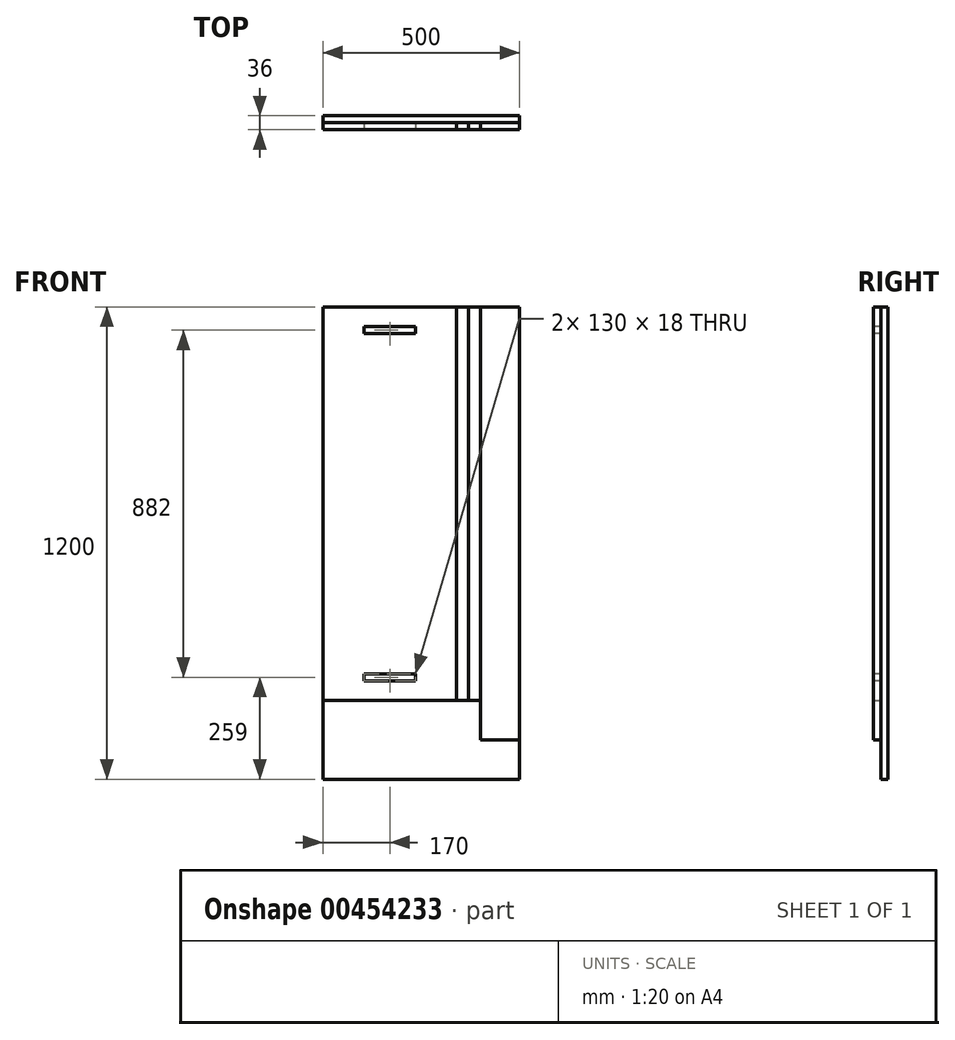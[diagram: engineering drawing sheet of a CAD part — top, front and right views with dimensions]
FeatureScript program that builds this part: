
annotation { "Feature Type Name" : "Feature", "Feature Type Description" : "" }
export const myFeature = defineFeature(function(context is Context, id is Id, definition is map)
    precondition{}
    {
        {
            var Q0;
            Q0=qCreatedBy(makeId("Front.planeOp"),FACE);
            var sketch = newSketch(context, id + "F0", { "sketchPlane" : qUnion([Q0])});
            skLineSegment(sketch, "E0.bottom", {"start": v(-250, -600) * mm, "end": v(250, -600) * mm});
            skLineSegment(sketch, "E0.top", {"start": v(-250, 600) * mm, "end": v(250, 600) * mm});
            skLineSegment(sketch, "E0.left", {"start": v(-250, -600) * mm, "end": v(-250, 600) * mm});
            skLineSegment(sketch, "E0.right", {"start": v(250, -600) * mm, "end": v(250, 600) * mm});
            skPoint(sketch, "E0.middle", {"position": v(0, 0) * mm});
            skSolve(sketch);
        }
        {
            var Q0;
            Q0=qSketchRegion(id+"F0",true);
            extrude(context, id + "F1", {"entities" : qUnion([Q0]), "depth" : 18 * mm});
        }
        {
            var Q0;
            Q0=makeQuery(id+"F1.opExtrude","CAP_FACE",FACE,{"disambiguationData":[OSD([sQuery(id+"F0.wireOp",EDGE,"E0.bottom"),sQuery(id+"F0.wireOp",EDGE,"E0.top"),sQuery(id+"F0.wireOp",EDGE,"E0.left"),sQuery(id+"F0.wireOp",EDGE,"E0.right")])],"isStart":false});
            var sketch = newSketch(context, id + "F2", { "sketchPlane" : qUnion([Q0])});
            skLineSegment(sketch, "E1.bottom", {"start": v(-250, 600) * mm, "end": v(90, 600) * mm});
            skLineSegment(sketch, "E1.top", {"start": v(-250, -400) * mm, "end": v(90, -400) * mm});
            skLineSegment(sketch, "E1.left", {"start": v(-250, 600) * mm, "end": v(-250, -400) * mm});
            skLineSegment(sketch, "E1.right", {"start": v(90, 600) * mm, "end": v(90, -400) * mm});
            skLineSegment(sketch, "E2.bottom", {"start": v(90, -400) * mm, "end": v(120, -400) * mm});
            skLineSegment(sketch, "E2.top", {"start": v(90, 600) * mm, "end": v(120, 600) * mm});
            skLineSegment(sketch, "E2.left", {"start": v(90, -400) * mm, "end": v(90, 600) * mm});
            skLineSegment(sketch, "E2.right", {"start": v(120, -400) * mm, "end": v(120, 600) * mm});
            skLineSegment(sketch, "E3.bottom", {"start": v(120, -400) * mm, "end": v(150, -400) * mm});
            skLineSegment(sketch, "E3.top", {"start": v(120, 600) * mm, "end": v(150, 600) * mm});
            skLineSegment(sketch, "E3.right", {"start": v(150, -400) * mm, "end": v(150, 600) * mm});
            skLineSegment(sketch, "E4.bottom", {"start": v(250, 600) * mm, "end": v(150, 600) * mm});
            skLineSegment(sketch, "E4.top", {"start": v(250, -500) * mm, "end": v(150, -500) * mm});
            skLineSegment(sketch, "E4.left", {"start": v(250, 600) * mm, "end": v(250, -500) * mm});
            skLineSegment(sketch, "E4.right", {"start": v(150, 600) * mm, "end": v(150, -500) * mm});
            skSolve(sketch);
        }
        {
            var Q0;
            Q0=makeQuery(id+"F2.imprint","IMPRINT",FACE,{"disambiguationData":[TD([[makeQuery(id+"F2.imprint","IMPRINT",EDGE,{"derivedFrom":sQuery(id+"F2.wireOp",EDGE,"E1.bottom")}),-1.0]])]});
            extrude(context, id + "F3", {"entities" : qUnion([Q0]), "depth" : 18 * mm});
        }
        {
            var Q0;
            Q0=makeQuery(id+"F2.imprint","IMPRINT",FACE,{"disambiguationData":[TD([[makeQuery(id+"F2.imprint","IMPRINT",EDGE,{"derivedFrom":sQuery(id+"F2.wireOp",EDGE,"E2.bottom")}),1.0]])]});
            extrude(context, id + "F4", {"entities" : qUnion([Q0]), "depth" : 18 * mm});
        }
        {
            var Q0;
            {var subQ0=sQuery(id+"F2.wireOp",EDGE,"E3.bottom");Q0=makeQuery(id+"F2.imprint","IMPRINT",FACE,{"disambiguationData":[TD([[makeQuery(id+"F2.imprint","IMPRINT",EDGE,{"derivedFrom":subQ0}),1.0]])]});}
            extrude(context, id + "F5", {"entities" : qUnion([Q0]), "depth" : 18 * mm});
        }
        {
            var Q0;
            {var subQ2=sQuery(id+"F2.wireOp",EDGE,"E4.bottom");Q0=makeQuery(id+"F2.imprint","IMPRINT",FACE,{"disambiguationData":[TD([[makeQuery(id+"F2.imprint","IMPRINT",EDGE,{"derivedFrom":subQ2}),-1.0]])]});}
            extrude(context, id + "F6", {"entities" : qUnion([Q0]), "depth" : 18 * mm});
        }
        {
            var Q0;
            Q0=makeQuery(id+"F3.opExtrude","CAP_FACE",FACE,{"disambiguationData":[OSD([sQuery(id+"F2.wireOp",EDGE,"E1.bottom"),sQuery(id+"F2.wireOp",EDGE,"E1.top"),sQuery(id+"F2.wireOp",EDGE,"E1.left"),sQuery(id+"F2.wireOp",EDGE,"E2.left")])],"isStart":false});
            var sketch = newSketch(context, id + "F7", { "sketchPlane" : qUnion([Q0])});
            skLineSegment(sketch, "E5.bottom", {"start": v(-145, 550) * mm, "end": v(-15, 550) * mm});
            skLineSegment(sketch, "E5.top", {"start": v(-145, 532) * mm, "end": v(-15, 532) * mm});
            skLineSegment(sketch, "E5.left", {"start": v(-145, 550) * mm, "end": v(-145, 532) * mm});
            skLineSegment(sketch, "E5.right", {"start": v(-15, 550) * mm, "end": v(-15, 532) * mm});
            skLineSegment(sketch, "E6", {"start": v(-250, 100) * mm, "end": v(90, 100) * mm, "construction": true});
            skLineSegment(sketch, "E7.MirrorCS", {"start": v(-15, -350) * mm, "end": v(-15, -332) * mm});
            skLineSegment(sketch, "E8.MirrorCS", {"start": v(-145, -350) * mm, "end": v(-145, -332) * mm});
            skLineSegment(sketch, "E9.MirrorCS", {"start": v(-145, -332) * mm, "end": v(-15, -332) * mm});
            skLineSegment(sketch, "E10.MirrorCS", {"start": v(-145, -350) * mm, "end": v(-15, -350) * mm});
            skLineSegment(sketch, "E11", {"start": v(-80, 600) * mm, "end": v(-80, 550) * mm});
            skSolve(sketch);
        }
        {
            var Q0;
            Q0=makeQuery(id+"F7.imprint","IMPRINT",FACE,{"disambiguationData":[TD([[makeQuery(id+"F7.imprint","IMPRINT",EDGE,{"derivedFrom":sQuery(id+"F7.wireOp",EDGE,"E5.bottom")}),-1.0]])]});
            var Q1;
            Q1=makeQuery(id+"F7.imprint","IMPRINT",FACE,{"disambiguationData":[TD([[makeQuery(id+"F7.imprint","IMPRINT",EDGE,{"derivedFrom":sQuery(id+"F7.wireOp",EDGE,"E7.MirrorCS")}),1.0]])]});
            var Q2;
            Q2=makeQuery(id+"F3.opExtrude","CAP_FACE",FACE,{"disambiguationData":[OSD([sQuery(id+"F2.wireOp",EDGE,"E1.bottom"),sQuery(id+"F2.wireOp",EDGE,"E1.top"),sQuery(id+"F2.wireOp",EDGE,"E1.left"),sQuery(id+"F2.wireOp",EDGE,"E2.left")])],"isStart":true});
            extrude(context, id + "F8", {"entities" : qUnion([Q0, Q1]), "operationType" : NewBodyOperationType.REMOVE, "endBound" : BoundingType.UP_TO_SURFACE, "oppositeDirection" : true, "endBoundEntityFace" : qUnion([Q2]), "depth" : 25 * mm});
        }
    });
